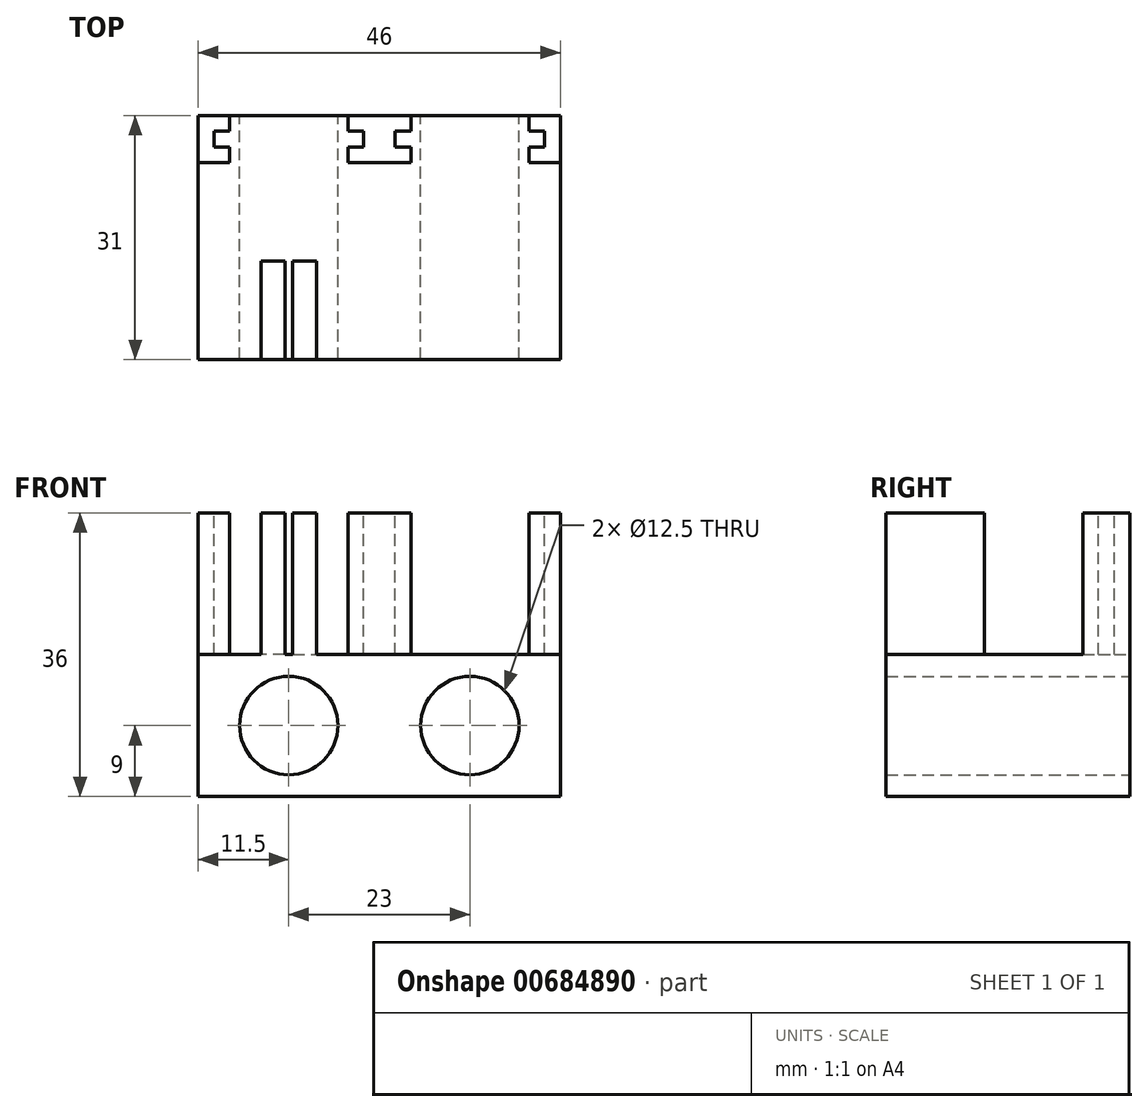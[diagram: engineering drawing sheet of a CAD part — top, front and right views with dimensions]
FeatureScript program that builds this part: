
annotation { "Feature Type Name" : "Feature", "Feature Type Description" : "" }
export const myFeature = defineFeature(function(context is Context, id is Id, definition is map)
    precondition{}
    {
        {
            var Q0;
            Q0=qCreatedBy(makeId("Front.planeOp"),FACE);
            var sketch = newSketch(context, id + "F0", { "sketchPlane" : qUnion([Q0])});
            skLineSegment(sketch, "E0.bottom", {"start": v(0, 0) * mm, "end": v(23, 0) * mm});
            skLineSegment(sketch, "E0.top", {"start": v(0, 18) * mm, "end": v(23, 18) * mm});
            skLineSegment(sketch, "E0.left", {"start": v(0, 0) * mm, "end": v(0, 18) * mm});
            skLineSegment(sketch, "E0.right", {"start": v(23, 0) * mm, "end": v(23, 18) * mm});
            skLineSegment(sketch, "E1", {"start": v(0, 9) * mm, "end": v(23, 9) * mm, "construction": true});
            skCircle(sketch, "E2", {"center": v(11.5, 9) * mm, "radius": 6.25 * mm});
            skLineSegment(sketch, "E3.bottom", {"start": v(0, 18) * mm, "end": v(4, 18) * mm});
            skLineSegment(sketch, "E3.top", {"start": v(0, 36) * mm, "end": v(4, 36) * mm});
            skLineSegment(sketch, "E3.left", {"start": v(0, 18) * mm, "end": v(0, 36) * mm});
            skLineSegment(sketch, "E3.right", {"start": v(4, 18) * mm, "end": v(4, 36) * mm});
            skLineSegment(sketch, "E4.bottom", {"start": v(23, 18) * mm, "end": v(19, 18) * mm});
            skLineSegment(sketch, "E4.top", {"start": v(23, 36) * mm, "end": v(19, 36) * mm});
            skLineSegment(sketch, "E4.left", {"start": v(23, 18) * mm, "end": v(23, 36) * mm});
            skLineSegment(sketch, "E4.right", {"start": v(19, 18) * mm, "end": v(19, 36) * mm});
            skLineSegment(sketch, "E5", {"start": v(4, 36) * mm, "end": v(19, 36) * mm, "construction": true});
            skSolve(sketch);
        }
        {
            var Q0;
            Q0 = qSketchRegion(id + "F0", true);
            extrude(context, id + "F1", {"entities" : qUnion([Q0]), "depth" : 6 * mm, "offsetDistance" : 25 * mm});
        }
        {
            var Q0;
            Q0=makeQuery(id+"F1.opExtrude","SWEPT_FACE",FACE,{"disambiguationData":[OSD([sQuery(id+"F0.wireOp",EDGE,"E3.top")])]});
            var sketch = newSketch(context, id + "F2", { "sketchPlane" : qUnion([Q0])});
            skLineSegment(sketch, "E6", {"start": v(4, -6) * mm, "end": v(4, -4) * mm, "construction": true});
            skLineSegment(sketch, "E7.bottom", {"start": v(4, -4) * mm, "end": v(2, -4) * mm});
            skLineSegment(sketch, "E7.top", {"start": v(4, -2) * mm, "end": v(2, -2) * mm});
            skLineSegment(sketch, "E7.left", {"start": v(4, -4) * mm, "end": v(4, -2) * mm});
            skLineSegment(sketch, "E7.right", {"start": v(2, -4) * mm, "end": v(2, -2) * mm});
            skSolve(sketch);
        }
        {
            var Q0;
            Q0=makeQuery(id+"F1.opExtrude","SWEPT_FACE",FACE,{"disambiguationData":[OSD([sQuery(id+"F0.wireOp",EDGE,"E4.top")])]});
            var sketch = newSketch(context, id + "F3", { "sketchPlane" : qUnion([Q0])});
            skLineSegment(sketch, "E8", {"start": v(19, -6) * mm, "end": v(19, -4) * mm, "construction": true});
            skLineSegment(sketch, "E9.bottom", {"start": v(19, -4) * mm, "end": v(21, -4) * mm});
            skLineSegment(sketch, "E9.top", {"start": v(19, -2) * mm, "end": v(21, -2) * mm});
            skLineSegment(sketch, "E9.left", {"start": v(19, -4) * mm, "end": v(19, -2) * mm});
            skLineSegment(sketch, "E9.right", {"start": v(21, -4) * mm, "end": v(21, -2) * mm});
            skSolve(sketch);
        }
        {
            var Q0;
            Q0=makeQuery(id+"F3.imprint","IMPRINT",FACE,{"disambiguationData":[TD([[makeQuery(id+"F3.imprint","IMPRINT",EDGE,{"derivedFrom":sQuery(id+"F3.wireOp",EDGE,"E9.bottom")}),1.0]])]});
            var Q1;
            Q1=makeQuery(id+"F2.imprint","IMPRINT",FACE,{"disambiguationData":[TD([[makeQuery(id+"F2.imprint","IMPRINT",EDGE,{"derivedFrom":sQuery(id+"F2.wireOp",EDGE,"E7.bottom")}),-1.0]])]});
            extrude(context, id + "F4", {"entities" : qUnion([Q0, Q1]), "operationType" : NewBodyOperationType.REMOVE, "oppositeDirection" : true, "depth" : 18 * mm, "offsetDistance" : 25 * mm});
        }
        {
            var Q0;
            Q0=makeQuery(id+"F1.opExtrude","CAP_FACE",FACE,{"disambiguationData":[OSD([sQuery(id+"F0.wireOp",EDGE,"E0.bottom"),sQuery(id+"F0.wireOp",EDGE,"E0.top"),sQuery(id+"F0.wireOp",EDGE,"E0.left"),sQuery(id+"F0.wireOp",EDGE,"E0.right"),sQuery(id+"F0.wireOp",EDGE,"E2"),sQuery(id+"F0.wireOp",EDGE,"E3.top"),sQuery(id+"F0.wireOp",EDGE,"E3.left"),sQuery(id+"F0.wireOp",EDGE,"E3.right"),sQuery(id+"F0.wireOp",EDGE,"E4.top"),sQuery(id+"F0.wireOp",EDGE,"E4.left"),sQuery(id+"F0.wireOp",EDGE,"E4.right")])],"isStart":false});
            var sketch = newSketch(context, id + "F5", { "sketchPlane" : qUnion([Q0])});
            skLineSegment(sketch, "E10", {"start": v(4, 18) * mm, "end": v(0, 18) * mm});
            skLineSegment(sketch, "E11", {"start": v(0, 18) * mm, "end": v(19, 18) * mm});
            skLineSegment(sketch, "E12", {"start": v(19, 18) * mm, "end": v(23, 18) * mm});
            skSolve(sketch);
        }
        {
            var Q0;
            {var subQ1=sQuery(id+"F5.wireOp",EDGE,"E12");Q0=makeQuery(id+"F5.imprint","IMPRINT",FACE,{"disambiguationData":[TD([[makeQuery(id+"F5.imprint","IMPRINT",EDGE,{"derivedFrom":subQ1}),-1.0]])]});}
            extrude(context, id + "F6", {"entities" : qUnion([Q0]), "operationType" : NewBodyOperationType.ADD, "depth" : 25 * mm, "offsetDistance" : 25 * mm});
        }
        {
            var Q0;
            Q0=makeQuery(id+"F1.opExtrude","SWEPT_BODY",BODY,{"disambiguationData":[OSD([sQuery(id+"F0.wireOp",EDGE,"E0.bottom"),sQuery(id+"F0.wireOp",EDGE,"E0.top"),sQuery(id+"F0.wireOp",EDGE,"E0.left"),sQuery(id+"F0.wireOp",EDGE,"E0.right"),sQuery(id+"F0.wireOp",EDGE,"E2"),sQuery(id+"F0.wireOp",EDGE,"E3.top"),sQuery(id+"F0.wireOp",EDGE,"E3.left"),sQuery(id+"F0.wireOp",EDGE,"E3.right"),sQuery(id+"F0.wireOp",EDGE,"E4.top"),sQuery(id+"F0.wireOp",EDGE,"E4.left"),sQuery(id+"F0.wireOp",EDGE,"E4.right")])]});
            var Q1;
            Q1=qCreatedBy(makeId("Right.planeOp"),FACE);
            mirror(context, id + "F7", {"operationType" : NewBodyOperationType.ADD, "entities" : qUnion([Q0]), "mirrorPlane" : qUnion([Q1])});
        }
        {
            var Q0;
            {var subQ0=makeQuery(id+"F6.boolean.opBoolean","MERGE",FACE,{"derivedFrom":[makeQuery(id+"F4.boolean.opBoolean","MERGE",FACE,{"derivedFrom":[makeQuery(id+"F1.opExtrude","SWEPT_FACE",FACE,{"disambiguationData":[OSD([sQuery(id+"F0.wireOp",EDGE,"E0.top")])]}),makeQuery(id+"F4.opExtrude","CAP_FACE",FACE,{"disambiguationData":[OSD([sQuery(id+"F2.wireOp",EDGE,"E7.bottom"),sQuery(id+"F2.wireOp",EDGE,"E7.top"),sQuery(id+"F2.wireOp",EDGE,"E7.left"),sQuery(id+"F2.wireOp",EDGE,"E7.right")])],"isStart":false}),makeQuery(id+"F4.opExtrude","CAP_FACE",FACE,{"disambiguationData":[OSD([sQuery(id+"F3.wireOp",EDGE,"E9.bottom"),sQuery(id+"F3.wireOp",EDGE,"E9.top"),sQuery(id+"F3.wireOp",EDGE,"E9.left"),sQuery(id+"F3.wireOp",EDGE,"E9.right")])],"isStart":false})]}),makeQuery(id+"F6.opExtrude","SWEPT_FACE",FACE,{"disambiguationData":[OSD([sQuery(id+"F5.wireOp",EDGE,"E11"),sQuery(id+"F5.wireOp",EDGE,"E12")])]})]});Q0=makeQuery(id+"F7.boolean.opBoolean","MERGE",FACE,{"derivedFrom":[subQ0,makeQuery(id+"F7.opPattern","COPY",FACE,{"derivedFrom":subQ0,"instanceName":"1"})]});}
            var sketch = newSketch(context, id + "F8", { "sketchPlane" : qUnion([Q0])});
            skLineSegment(sketch, "E13", {"start": v(-19, -6) * mm, "end": v(-4, -6) * mm, "construction": true});
            skLineSegment(sketch, "E14", {"start": v(4, -6) * mm, "end": v(19, -6) * mm, "construction": true});
            skLineSegment(sketch, "E15", {"start": v(-11.5, -6) * mm, "end": v(-11.5, -31) * mm, "construction": true});
            skLineSegment(sketch, "E16", {"start": v(11.5, -6) * mm, "end": v(11.5, -31) * mm, "construction": true});
            skLineSegment(sketch, "E17", {"start": v(-12, -18.5) * mm, "end": v(-12, -31) * mm});
            skLineSegment(sketch, "E18", {"start": v(-11, -18.5) * mm, "end": v(-11, -31) * mm});
            skLineSegment(sketch, "E19", {"start": v(-12, -18.5) * mm, "end": v(-15, -18.5) * mm});
            skLineSegment(sketch, "E20", {"start": v(-15, -18.5) * mm, "end": v(-15, -31) * mm});
            skLineSegment(sketch, "E21", {"start": v(-11, -18.5) * mm, "end": v(-8, -18.5) * mm});
            skLineSegment(sketch, "E22", {"start": v(-8, -31) * mm, "end": v(-11, -31) * mm});
            skLineSegment(sketch, "E23", {"start": v(-8, -31) * mm, "end": v(-8, -18.5) * mm});
            skSolve(sketch);
        }
        {
            var Q0;
            {var subQ0=sQuery(id+"F8.wireOp",EDGE,"E17");Q0=makeQuery(id+"F8.imprint","IMPRINT",FACE,{"disambiguationData":[TD([[makeQuery(id+"F8.imprint","IMPRINT",EDGE,{"derivedFrom":subQ0}),-1.0]])]});}
            var Q1;
            Q1=makeQuery(id+"F8.imprint","IMPRINT",FACE,{"disambiguationData":[TD([[makeQuery(id+"F8.imprint","IMPRINT",EDGE,{"derivedFrom":sQuery(id+"F8.wireOp",EDGE,"E18")}),1.0]])]});
            extrude(context, id + "F9", {"entities" : qUnion([Q0, Q1]), "operationType" : NewBodyOperationType.ADD, "depth" : 18 * mm, "offsetDistance" : 25 * mm});
        }
    });
